# Revit family: 0048704 Sylvania Lighting Fixture SYLPRF SUP LED G3 1200MM T 4K E3
name_source: partatom
category: Lighting Fixtures
revit_build: Autodesk Revit 2016 (Build: 20150220_1215(x64)
units: mm (PartAtom-declared; Revit-internal decimal feet)

## family parameters
Cut with Voids When Loaded = No
Host = Face
Light Source = Yes
OmniClass Number = 23.80.70.11.14
OmniClass Title = General Luminaries, Directional
Part Type = Normal
Room Calculation Point = No
Round Connector Dimension = Use Diameter
Shared = No

## types (2) — shared parameters
AccessoryMaterial = Diffuser-Sylvania-Glow
Assembly Code = D5020200
AssetType = Fixed
BodyMaterial = Body-Sylvania-Gray
ClassificationName = Uniclass2015
ClassificationValue = EF_70_80
Color Filter = 16777215
Default Elevation = 1219 mm
Description = Sylproof Superia, integrated LED weatherproof luminaire, with UV stabilized flat diffuser and linear prisms designed to achieve uniform lit appearance, optimise light output and to reduce glare, stainless steel diffuser clips and fixing brackets for surface and wall mounting. L 1278 mm x W 110 mm x H 78 mm size, Polycarbonate housing, Polycarbonate diffuser, Non dimmable,   3 hour emergency, 4000K, CRI80,  5400 lm, 38 W, 140 lm/W, nominal average life (h):50000, energy class: A++ A+ A Class I,IK08, IP65.
DiffuserMaterial = Diffuser-Sylvania-Transparent
Dimming Lamp Color Temperature Shift = <None>
DimmingControlOptions = Non dimmable
DocumentationLiterature = http://www.sylvania-lighting.com
DurationUnit = hours
ElectricShockClassification = Class I
Emit Shape Visible in Rendering = No
Emit from Rectangle Length = 1252 mm  [stored 4.10761 ft]
Emit from Rectangle Width = 90 mm  [stored 0.295276 ft]
ExpectedLife = 50000
IfcExportAs = IfcLightFixtureType
IfcExportType = IfcLightFixtureType
ImpactProtectionIndex = IK08
IngressProtection = IP65
InputNominalFrequency = 50/60 Hz
InputVoltage = 220-240V~
Keynote = 16500
Lamp = LED
LampColourRenderingIndex = 80
LampColourTemperature = 4000 K
LampMacAdamStep = 3
LampsType = LED
Length = 1272 mm  [stored 4.17323 ft]
LuminousEfficacy = 140 lm/W
Manufacturer = Feilo Sylvania
ManufacturerName = Feilo Sylvania
Material = polycarbonate housing, polycarbonate diffuser
Model = SYLPRF SUP LED G3 1200MM T 4K E3
ModelNumber = 0048704
ModelReference = SYLPRF SUP LED G3 1200MM T 4K E3
Name = SYLPRF SUP LED G3 1200MM T 4K E3
NominalHeight = 78 mm  [stored 0.255906 ft]
NominalLength = 1278 mm  [stored 4.19291 ft]
ReflectorMaterial = <By Category>
Tilt Angle = -90.00°
Type Image = <None>
TypeName = SYLPRF SUP LED G3 1200MM T 4K E3
URL = http://www.sylvania-lighting.com
Voltage = 230 V
Weight = 2.18 kg
Width = 110 mm  [stored 0.360892 ft]
zero-valued in all types: Cost, NominalWidth, PowerFactor

## per-type parameters (varying)
| type | Apparent Load | LampNominalLuminous | Photometric Web File | PowerConsumption |
| 0048704 SYLPRF SUP LED G3 1200MM T 4K E3 | 38 VA | 5400 lm | 0048704.ies | 38 W |
| 0048704 SYLPRF SUP LED G3 1200MM T 4K E3 Emergency mode | 2 VA | 240 lm | 0048704EM.ies | 1.71 W |

note: [stored X ft] marks values corroborated as IEEE doubles in the binary element streams (Revit-internal decimal feet)

## geometry (parser evidence)
native form markers: Sweep x2
no freeform markers — native parametric forms only
